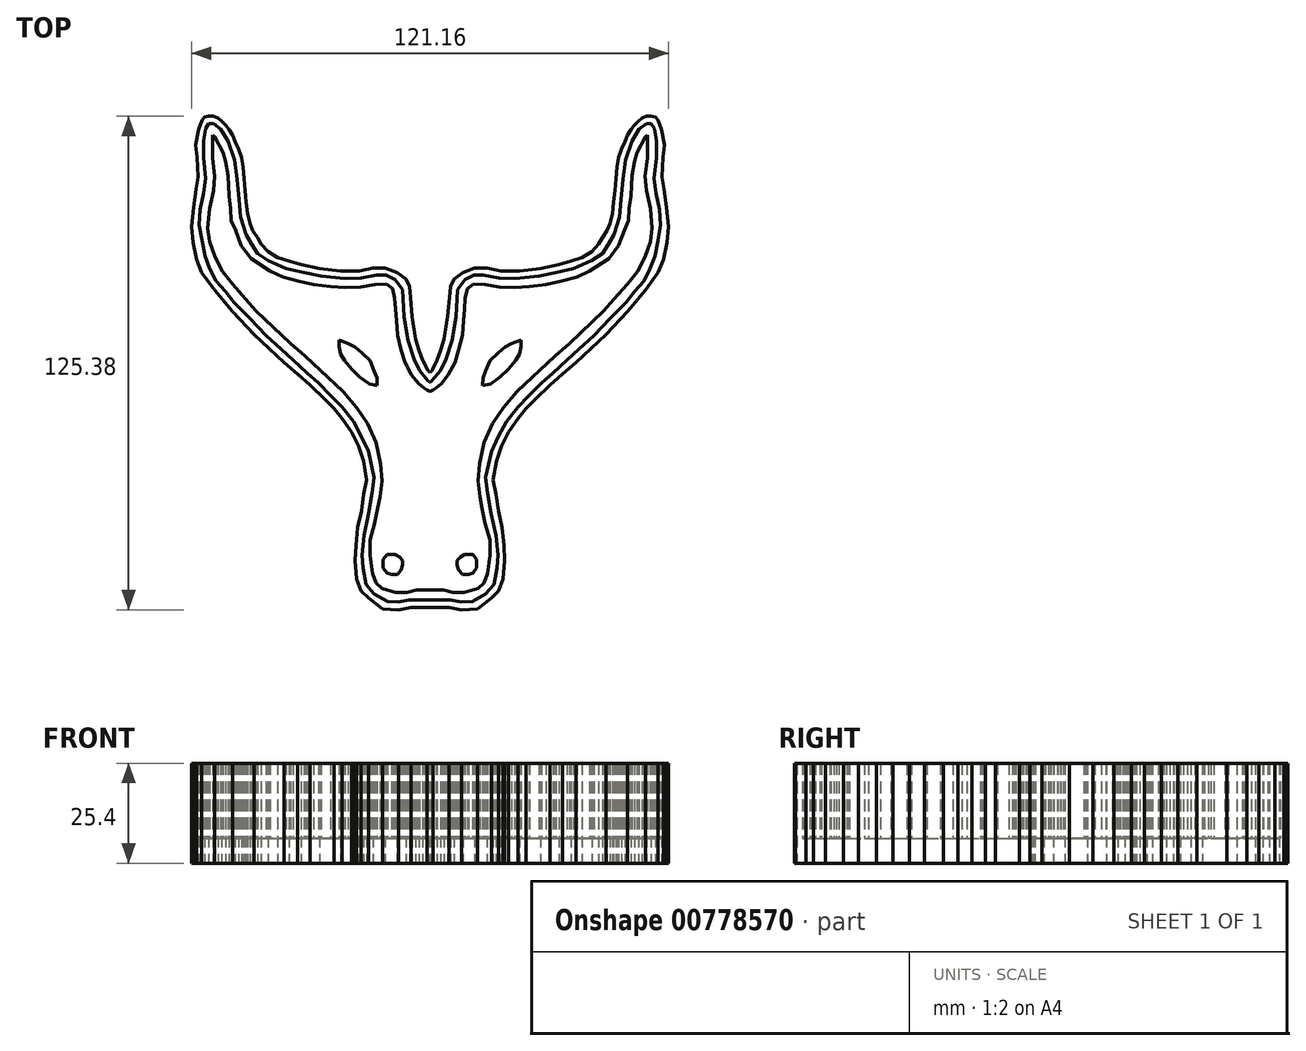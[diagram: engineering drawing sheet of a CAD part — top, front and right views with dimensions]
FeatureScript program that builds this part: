
annotation { "Feature Type Name" : "Feature", "Feature Type Description" : "" }
export const myFeature = defineFeature(function(context is Context, id is Id, definition is map)
    precondition{}
    {
        {
            var Q0;
            Q0=qCreatedBy(makeId("Top.planeOp"),FACE);
            var sketch = newSketch(context, id + "F0", { "sketchPlane" : qUnion([Q0])});
            skLineSegment(sketch, "E0", {"start": v(0, -62.65) * mm, "end": v(0.74, -62.65) * mm});
            skLineSegment(sketch, "E1", {"start": v(0.74, -62.65) * mm, "end": v(4.87, -62.73) * mm});
            skLineSegment(sketch, "E2", {"start": v(4.87, -62.73) * mm, "end": v(7.96, -63.29) * mm});
            skLineSegment(sketch, "E3", {"start": v(7.96, -63.29) * mm, "end": v(12.06, -63.03) * mm});
            skLineSegment(sketch, "E4", {"start": v(12.06, -63.03) * mm, "end": v(15.62, -60.34) * mm});
            skLineSegment(sketch, "E5", {"start": v(15.62, -60.34) * mm, "end": v(17.47, -58.47) * mm});
            skLineSegment(sketch, "E6", {"start": v(17.47, -58.47) * mm, "end": v(18.6, -55.45) * mm});
            skLineSegment(sketch, "E7", {"start": v(18.6, -55.45) * mm, "end": v(19, -50.76) * mm});
            skLineSegment(sketch, "E8", {"start": v(19, -50.76) * mm, "end": v(18.78, -46.99) * mm});
            skLineSegment(sketch, "E9", {"start": v(18.78, -46.99) * mm, "end": v(18.36, -42.4) * mm});
            skLineSegment(sketch, "E10", {"start": v(18.36, -42.4) * mm, "end": v(17.38, -38.24) * mm});
            skLineSegment(sketch, "E11", {"start": v(17.38, -38.24) * mm, "end": v(16.84, -34.03) * mm});
            skLineSegment(sketch, "E12", {"start": v(16.84, -34.03) * mm, "end": v(16.08, -30.27) * mm});
            skLineSegment(sketch, "E13", {"start": v(16.08, -30.27) * mm, "end": v(16.93, -25.47) * mm});
            skLineSegment(sketch, "E14", {"start": v(16.93, -25.47) * mm, "end": v(18.14, -21.7) * mm});
            skLineSegment(sketch, "E15", {"start": v(18.14, -21.7) * mm, "end": v(19.93, -18.19) * mm});
            skLineSegment(sketch, "E16", {"start": v(19.93, -18.19) * mm, "end": v(22.34, -14.72) * mm});
            skLineSegment(sketch, "E17", {"start": v(22.34, -14.72) * mm, "end": v(24.35, -12.2) * mm});
            skLineSegment(sketch, "E18", {"start": v(24.35, -12.2) * mm, "end": v(26.71, -9.89) * mm});
            skLineSegment(sketch, "E19", {"start": v(26.71, -9.89) * mm, "end": v(30.5, -6.18) * mm});
            skLineSegment(sketch, "E20", {"start": v(30.5, -6.18) * mm, "end": v(33.6, -3.4) * mm});
            skLineSegment(sketch, "E21", {"start": v(33.6, -3.4) * mm, "end": v(37.06, -0.45) * mm});
            skLineSegment(sketch, "E22", {"start": v(37.06, -0.45) * mm, "end": v(44.75, 6.6) * mm});
            skLineSegment(sketch, "E23", {"start": v(44.75, 6.6) * mm, "end": v(50.18, 12.54) * mm});
            skLineSegment(sketch, "E24", {"start": v(50.18, 12.54) * mm, "end": v(54.75, 17.93) * mm});
            skLineSegment(sketch, "E25", {"start": v(54.75, 17.93) * mm, "end": v(57.98, 22.34) * mm});
            skLineSegment(sketch, "E26", {"start": v(57.98, 22.34) * mm, "end": v(59.34, 25.63) * mm});
            skLineSegment(sketch, "E27", {"start": v(59.34, 25.63) * mm, "end": v(60.16, 30.02) * mm});
            skLineSegment(sketch, "E28", {"start": v(60.16, 30.02) * mm, "end": v(60.58, 34.11) * mm});
            skLineSegment(sketch, "E29", {"start": v(60.58, 34.11) * mm, "end": v(60.1, 38.93) * mm});
            skLineSegment(sketch, "E30", {"start": v(60.1, 38.93) * mm, "end": v(59.4, 43.55) * mm});
            skLineSegment(sketch, "E31", {"start": v(59.4, 43.55) * mm, "end": v(58.97, 46.63) * mm});
            skLineSegment(sketch, "E32", {"start": v(58.97, 46.63) * mm, "end": v(59.15, 51.67) * mm});
            skLineSegment(sketch, "E33", {"start": v(59.15, 51.67) * mm, "end": v(59.6, 54.77) * mm});
            skLineSegment(sketch, "E34", {"start": v(59.6, 54.77) * mm, "end": v(58.85, 58.77) * mm});
            skLineSegment(sketch, "E35", {"start": v(58.85, 58.77) * mm, "end": v(57.94, 61.11) * mm});
            skLineSegment(sketch, "E36", {"start": v(57.94, 61.11) * mm, "end": v(57.23, 61.84) * mm});
            skLineSegment(sketch, "E37", {"start": v(57.23, 61.84) * mm, "end": v(56.19, 62.09) * mm});
            skLineSegment(sketch, "E38", {"start": v(56.19, 62.09) * mm, "end": v(55.06, 62.09) * mm});
            skLineSegment(sketch, "E39", {"start": v(55.06, 62.09) * mm, "end": v(53.9, 61.63) * mm});
            skLineSegment(sketch, "E40", {"start": v(53.9, 61.63) * mm, "end": v(52.95, 60.92) * mm});
            skLineSegment(sketch, "E41", {"start": v(52.95, 60.92) * mm, "end": v(51.9, 59.9) * mm});
            skLineSegment(sketch, "E42", {"start": v(51.9, 59.9) * mm, "end": v(51.01, 58.77) * mm});
            skLineSegment(sketch, "E43", {"start": v(51.01, 58.77) * mm, "end": v(50.17, 57.35) * mm});
            skLineSegment(sketch, "E44", {"start": v(50.17, 57.35) * mm, "end": v(49.52, 55.7) * mm});
            skLineSegment(sketch, "E45", {"start": v(49.52, 55.7) * mm, "end": v(48.62, 53.78) * mm});
            skLineSegment(sketch, "E46", {"start": v(48.62, 53.78) * mm, "end": v(47.9, 51.57) * mm});
            skLineSegment(sketch, "E47", {"start": v(47.9, 51.57) * mm, "end": v(47.46, 49.14) * mm});
            skLineSegment(sketch, "E48", {"start": v(47.46, 49.14) * mm, "end": v(47.2, 46.3) * mm});
            skLineSegment(sketch, "E49", {"start": v(47.2, 46.3) * mm, "end": v(46.94, 43.22) * mm});
            skLineSegment(sketch, "E50", {"start": v(46.94, 43.22) * mm, "end": v(46.7, 40.3) * mm});
            skLineSegment(sketch, "E51", {"start": v(46.7, 40.3) * mm, "end": v(46.39, 37.4) * mm});
            skLineSegment(sketch, "E52", {"start": v(46.39, 37.4) * mm, "end": v(45.73, 34.8) * mm});
            skLineSegment(sketch, "E53", {"start": v(45.73, 34.8) * mm, "end": v(45.03, 33.04) * mm});
            skLineSegment(sketch, "E54", {"start": v(45.03, 33.04) * mm, "end": v(43.83, 31.24) * mm});
            skLineSegment(sketch, "E55", {"start": v(43.83, 31.24) * mm, "end": v(42.87, 29.66) * mm});
            skLineSegment(sketch, "E56", {"start": v(42.87, 29.66) * mm, "end": v(41.16, 27.69) * mm});
            skLineSegment(sketch, "E57", {"start": v(41.16, 27.69) * mm, "end": v(38.68, 26.24) * mm});
            skLineSegment(sketch, "E58", {"start": v(38.68, 26.24) * mm, "end": v(35.85, 25.34) * mm});
            skLineSegment(sketch, "E59", {"start": v(35.85, 25.34) * mm, "end": v(32.72, 24.46) * mm});
            skLineSegment(sketch, "E60", {"start": v(32.72, 24.46) * mm, "end": v(28.06, 23.4) * mm});
            skLineSegment(sketch, "E61", {"start": v(28.06, 23.4) * mm, "end": v(22.72, 22.8) * mm});
            skLineSegment(sketch, "E62", {"start": v(22.72, 22.8) * mm, "end": v(18.07, 22.8) * mm});
            skLineSegment(sketch, "E63", {"start": v(18.07, 22.8) * mm, "end": v(14.47, 23.58) * mm});
            skLineSegment(sketch, "E64", {"start": v(14.47, 23.58) * mm, "end": v(11.36, 23.58) * mm});
            skLineSegment(sketch, "E65", {"start": v(11.36, 23.58) * mm, "end": v(8.37, 22.4) * mm});
            skLineSegment(sketch, "E66", {"start": v(8.37, 22.4) * mm, "end": v(6.11, 20.67) * mm});
            skLineSegment(sketch, "E67", {"start": v(6.11, 20.67) * mm, "end": v(5.22, 18.85) * mm});
            skLineSegment(sketch, "E68", {"start": v(5.22, 18.85) * mm, "end": v(4.92, 15.98) * mm});
            skLineSegment(sketch, "E69", {"start": v(4.52, 11.15) * mm, "end": v(3.62, 5.47) * mm});
            skLineSegment(sketch, "E70", {"start": v(3.62, 5.47) * mm, "end": v(2.73, 2.52) * mm});
            skLineSegment(sketch, "E71", {"start": v(2.73, 2.52) * mm, "end": v(1.85, 0.16) * mm});
            skLineSegment(sketch, "E72", {"start": v(1.85, 0.16) * mm, "end": v(0.64, -2.23) * mm});
            skLineSegment(sketch, "E73", {"start": v(0.64, -2.23) * mm, "end": v(0.34, -2.71) * mm});
            skLineSegment(sketch, "E74", {"start": v(0.34, -2.71) * mm, "end": v(0, -2.85) * mm});
            skLineSegment(sketch, "E75", {"start": v(4.52, 11.15) * mm, "end": v(4.92, 15.98) * mm});
            skLineSegment(sketch, "E76", {"start": v(13.4, -6.26) * mm, "end": v(15.4, -5.94) * mm});
            skLineSegment(sketch, "E77", {"start": v(15.4, -5.94) * mm, "end": v(17.85, -4.1) * mm});
            skLineSegment(sketch, "E78", {"start": v(17.85, -4.1) * mm, "end": v(19.98, -2.1) * mm});
            skLineSegment(sketch, "E79", {"start": v(19.98, -2.1) * mm, "end": v(21.74, 0) * mm});
            skLineSegment(sketch, "E80", {"start": v(21.74, 0) * mm, "end": v(22.7, 1.68) * mm});
            skLineSegment(sketch, "E81", {"start": v(22.7, 1.68) * mm, "end": v(23.14, 3.64) * mm});
            skLineSegment(sketch, "E82", {"start": v(23.14, 3.64) * mm, "end": v(23.14, 5.28) * mm});
            skLineSegment(sketch, "E83", {"start": v(23.14, 5.28) * mm, "end": v(20.78, 4.36) * mm});
            skLineSegment(sketch, "E84", {"start": v(20.78, 4.36) * mm, "end": v(19.02, 3.52) * mm});
            skLineSegment(sketch, "E85", {"start": v(19.02, 3.52) * mm, "end": v(17.25, 1.92) * mm});
            skLineSegment(sketch, "E86", {"start": v(17.25, 1.92) * mm, "end": v(15.25, 0) * mm});
            skLineSegment(sketch, "E87", {"start": v(15.25, 0) * mm, "end": v(14.17, -2.57) * mm});
            skLineSegment(sketch, "E88", {"start": v(14.17, -2.57) * mm, "end": v(13.48, -4.42) * mm});
            skLineSegment(sketch, "E89", {"start": v(13.48, -4.42) * mm, "end": v(13.4, -6.26) * mm});
            skLineSegment(sketch, "E90", {"start": v(8.83, -49.27) * mm, "end": v(10.95, -49.27) * mm});
            skLineSegment(sketch, "E91", {"start": v(10.95, -49.27) * mm, "end": v(11.86, -50.52) * mm});
            skLineSegment(sketch, "E92", {"start": v(11.86, -50.52) * mm, "end": v(11.86, -52.64) * mm});
            skLineSegment(sketch, "E93", {"start": v(11.86, -52.64) * mm, "end": v(10.95, -54) * mm});
            skLineSegment(sketch, "E94", {"start": v(10.95, -54) * mm, "end": v(9.74, -54.3) * mm});
            skLineSegment(sketch, "E95", {"start": v(9.74, -54.3) * mm, "end": v(8.22, -54.3) * mm});
            skLineSegment(sketch, "E96", {"start": v(8.22, -54.3) * mm, "end": v(7.31, -53.18) * mm});
            skLineSegment(sketch, "E97", {"start": v(7.31, -53.18) * mm, "end": v(6.9, -51.93) * mm});
            skLineSegment(sketch, "E98", {"start": v(6.9, -51.93) * mm, "end": v(6.9, -50.72) * mm});
            skLineSegment(sketch, "E99", {"start": v(6.9, -50.72) * mm, "end": v(7.75, -49.88) * mm});
            skLineSegment(sketch, "E100", {"start": v(7.75, -49.88) * mm, "end": v(8.83, -49.27) * mm});
            skLineSegment(sketch, "E101", {"start": v(0, -58.26) * mm, "end": v(3.39, -58.26) * mm});
            skLineSegment(sketch, "E102", {"start": v(3.39, -58.26) * mm, "end": v(5.83, -58.91) * mm});
            skLineSegment(sketch, "E103", {"start": v(5.83, -58.91) * mm, "end": v(8.72, -58.91) * mm});
            skLineSegment(sketch, "E104", {"start": v(8.72, -58.91) * mm, "end": v(12.18, -57.92) * mm});
            skLineSegment(sketch, "E105", {"start": v(12.18, -57.92) * mm, "end": v(13.68, -56.45) * mm});
            skLineSegment(sketch, "E106", {"start": v(13.68, -56.45) * mm, "end": v(14.61, -54.04) * mm});
            skLineSegment(sketch, "E107", {"start": v(14.61, -54.04) * mm, "end": v(15.24, -49.5) * mm});
            skLineSegment(sketch, "E108", {"start": v(15.24, -49.5) * mm, "end": v(15.24, -45.5) * mm});
            skLineSegment(sketch, "E109", {"start": v(15.24, -45.5) * mm, "end": v(14.06, -41.39) * mm});
            skLineSegment(sketch, "E110", {"start": v(14.06, -41.39) * mm, "end": v(13.28, -37.6) * mm});
            skLineSegment(sketch, "E111", {"start": v(13.28, -37.6) * mm, "end": v(12.71, -34.68) * mm});
            skLineSegment(sketch, "E112", {"start": v(12.71, -34.68) * mm, "end": v(12.18, -30.57) * mm});
            skLineSegment(sketch, "E113", {"start": v(12.18, -30.57) * mm, "end": v(12.57, -26.2) * mm});
            skLineSegment(sketch, "E114", {"start": v(12.57, -26.2) * mm, "end": v(13.68, -20.73) * mm});
            skLineSegment(sketch, "E115", {"start": v(13.68, -20.73) * mm, "end": v(15.92, -16) * mm});
            skLineSegment(sketch, "E116", {"start": v(15.92, -16) * mm, "end": v(18.67, -11.86) * mm});
            skLineSegment(sketch, "E117", {"start": v(18.67, -11.86) * mm, "end": v(22.07, -7.86) * mm});
            skLineSegment(sketch, "E118", {"start": v(22.07, -7.86) * mm, "end": v(25.8, -4.35) * mm});
            skLineSegment(sketch, "E119", {"start": v(25.8, -4.35) * mm, "end": v(28.59, -1.74) * mm});
            skLineSegment(sketch, "E120", {"start": v(28.59, -1.74) * mm, "end": v(31.74, 1.23) * mm});
            skLineSegment(sketch, "E121", {"start": v(31.74, 1.23) * mm, "end": v(35.39, 4.35) * mm});
            skLineSegment(sketch, "E122", {"start": v(35.39, 4.35) * mm, "end": v(39.8, 8.5) * mm});
            skLineSegment(sketch, "E123", {"start": v(39.8, 8.5) * mm, "end": v(44.15, 12.58) * mm});
            skLineSegment(sketch, "E124", {"start": v(44.15, 12.58) * mm, "end": v(46.78, 15.6) * mm});
            skLineSegment(sketch, "E125", {"start": v(46.78, 15.6) * mm, "end": v(50.13, 19.4) * mm});
            skLineSegment(sketch, "E126", {"start": v(50.13, 19.4) * mm, "end": v(52.7, 22.66) * mm});
            skLineSegment(sketch, "E127", {"start": v(52.7, 22.66) * mm, "end": v(54.6, 26.35) * mm});
            skLineSegment(sketch, "E128", {"start": v(54.6, 26.35) * mm, "end": v(56.02, 30.32) * mm});
            skLineSegment(sketch, "E129", {"start": v(56.02, 30.32) * mm, "end": v(56.45, 33.75) * mm});
            skLineSegment(sketch, "E130", {"start": v(56.45, 33.75) * mm, "end": v(56.02, 38.6) * mm});
            skLineSegment(sketch, "E131", {"start": v(56.02, 38.6) * mm, "end": v(55, 43.24) * mm});
            skLineSegment(sketch, "E132", {"start": v(55, 43.24) * mm, "end": v(54.69, 46.85) * mm});
            skLineSegment(sketch, "E133", {"start": v(54.69, 46.85) * mm, "end": v(55.29, 51.46) * mm});
            skLineSegment(sketch, "E134", {"start": v(55.29, 51.46) * mm, "end": v(55.29, 54.8) * mm});
            skLineSegment(sketch, "E135", {"start": v(55.29, 54.8) * mm, "end": v(55.29, 57.3) * mm});
            skLineSegment(sketch, "E136", {"start": v(55.29, 57.3) * mm, "end": v(54.78, 56.96) * mm});
            skLineSegment(sketch, "E137", {"start": v(54.78, 56.96) * mm, "end": v(53.87, 55.29) * mm});
            skLineSegment(sketch, "E138", {"start": v(53.87, 55.29) * mm, "end": v(52.55, 52.86) * mm});
            skLineSegment(sketch, "E139", {"start": v(52.55, 52.86) * mm, "end": v(51.97, 50.53) * mm});
            skLineSegment(sketch, "E140", {"start": v(51.97, 50.53) * mm, "end": v(51.3, 46.98) * mm});
            skLineSegment(sketch, "E141", {"start": v(51.3, 46.98) * mm, "end": v(51.02, 41.84) * mm});
            skLineSegment(sketch, "E142", {"start": v(51.02, 41.84) * mm, "end": v(50.62, 38.65) * mm});
            skLineSegment(sketch, "E143", {"start": v(50.62, 38.65) * mm, "end": v(50.46, 35.6) * mm});
            skLineSegment(sketch, "E144", {"start": v(50.46, 35.6) * mm, "end": v(49.38, 33.15) * mm});
            skLineSegment(sketch, "E145", {"start": v(49.38, 33.15) * mm, "end": v(47.94, 29.21) * mm});
            skLineSegment(sketch, "E146", {"start": v(47.94, 29.21) * mm, "end": v(45.51, 25.93) * mm});
            skLineSegment(sketch, "E147", {"start": v(45.51, 25.93) * mm, "end": v(40.56, 22.72) * mm});
            skLineSegment(sketch, "E148", {"start": v(40.56, 22.72) * mm, "end": v(37.33, 21.28) * mm});
            skLineSegment(sketch, "E149", {"start": v(37.33, 21.28) * mm, "end": v(33.44, 20.23) * mm});
            skLineSegment(sketch, "E150", {"start": v(33.44, 20.23) * mm, "end": v(29.54, 19.3) * mm});
            skLineSegment(sketch, "E151", {"start": v(29.54, 19.3) * mm, "end": v(25.31, 18.86) * mm});
            skLineSegment(sketch, "E152", {"start": v(25.31, 18.86) * mm, "end": v(21.54, 18.56) * mm});
            skLineSegment(sketch, "E153", {"start": v(21.54, 18.56) * mm, "end": v(17.66, 18.76) * mm});
            skLineSegment(sketch, "E154", {"start": v(17.66, 18.76) * mm, "end": v(13.99, 19.32) * mm});
            skLineSegment(sketch, "E155", {"start": v(13.99, 19.32) * mm, "end": v(11.07, 19.47) * mm});
            skLineSegment(sketch, "E156", {"start": v(11.07, 19.47) * mm, "end": v(9.48, 18.3) * mm});
            skLineSegment(sketch, "E157", {"start": v(9.48, 18.3) * mm, "end": v(8.94, 15.89) * mm});
            skLineSegment(sketch, "E158", {"start": v(8.94, 15.89) * mm, "end": v(8.8, 13.1) * mm});
            skLineSegment(sketch, "E159", {"start": v(8.8, 13.1) * mm, "end": v(8.48, 10.24) * mm});
            skLineSegment(sketch, "E160", {"start": v(8.48, 10.24) * mm, "end": v(8.28, 6.5) * mm});
            skLineSegment(sketch, "E161", {"start": v(8.28, 6.5) * mm, "end": v(7.31, 2.66) * mm});
            skLineSegment(sketch, "E162", {"start": v(7.31, 2.66) * mm, "end": v(6.37, -0.49) * mm});
            skLineSegment(sketch, "E163", {"start": v(6.37, -0.49) * mm, "end": v(4.65, -3.6) * mm});
            skLineSegment(sketch, "E164", {"start": v(4.65, -3.6) * mm, "end": v(2.89, -5.84) * mm});
            skLineSegment(sketch, "E165", {"start": v(2.89, -5.84) * mm, "end": v(1.52, -6.98) * mm});
            skLineSegment(sketch, "E166", {"start": v(1.52, -6.98) * mm, "end": v(0.76, -7.52) * mm});
            skLineSegment(sketch, "E167", {"start": v(0.76, -7.52) * mm, "end": v(0, -7.9) * mm});
            skLineSegment(sketch, "E168", {"start": v(0, 69.58) * mm, "end": v(0, -68.29) * mm, "construction": true});
            skLineSegment(sketch, "E169.MirrorCS", {"start": v(-0.64, -2.23) * mm, "end": v(-0.34, -2.71) * mm});
            skLineSegment(sketch, "E170.MirrorCS", {"start": v(-0.34, -2.71) * mm, "end": v(0, -2.85) * mm});
            skLineSegment(sketch, "E171.MirrorCS", {"start": v(-1.85, 0.16) * mm, "end": v(-0.64, -2.23) * mm});
            skLineSegment(sketch, "E172.MirrorCS", {"start": v(-55.29, 57.3) * mm, "end": v(-54.78, 56.96) * mm});
            skLineSegment(sketch, "E173.MirrorCS", {"start": v(-9.48, 18.3) * mm, "end": v(-8.94, 15.89) * mm});
            skLineSegment(sketch, "E174.MirrorCS", {"start": v(-56.19, 62.09) * mm, "end": v(-55.06, 62.09) * mm});
            skLineSegment(sketch, "E175.MirrorCS", {"start": v(-52.95, 60.92) * mm, "end": v(-51.9, 59.9) * mm});
            skLineSegment(sketch, "E176.MirrorCS", {"start": v(-55.06, 62.09) * mm, "end": v(-53.9, 61.63) * mm});
            skLineSegment(sketch, "E177.MirrorCS", {"start": v(-53.9, 61.63) * mm, "end": v(-52.95, 60.92) * mm});
            skLineSegment(sketch, "E178.MirrorCS", {"start": v(-51.9, 59.9) * mm, "end": v(-51.01, 58.77) * mm});
            skLineSegment(sketch, "E179.MirrorCS", {"start": v(-57.98, 22.34) * mm, "end": v(-59.34, 25.63) * mm});
            skLineSegment(sketch, "E180.MirrorCS", {"start": v(-8.83, -49.27) * mm, "end": v(-10.95, -49.27) * mm});
            skLineSegment(sketch, "E181.MirrorCS", {"start": v(-51.01, 58.77) * mm, "end": v(-50.17, 57.35) * mm});
            skLineSegment(sketch, "E182.MirrorCS", {"start": v(-10.95, -49.27) * mm, "end": v(-11.86, -50.52) * mm});
            skLineSegment(sketch, "E183.MirrorCS", {"start": v(-12.06, -63.03) * mm, "end": v(-15.62, -60.34) * mm});
            skLineSegment(sketch, "E184.MirrorCS", {"start": v(-15.62, -60.34) * mm, "end": v(-17.47, -58.47) * mm});
            skLineSegment(sketch, "E185.MirrorCS", {"start": v(-11.86, -50.52) * mm, "end": v(-11.86, -52.64) * mm});
            skLineSegment(sketch, "E186.MirrorCS", {"start": v(-17.47, -58.47) * mm, "end": v(-18.6, -55.45) * mm});
            skLineSegment(sketch, "E187.MirrorCS", {"start": v(-18.6, -55.45) * mm, "end": v(-19, -50.76) * mm});
            skLineSegment(sketch, "E188.MirrorCS", {"start": v(-50.17, 57.35) * mm, "end": v(-49.52, 55.7) * mm});
            skLineSegment(sketch, "E189.MirrorCS", {"start": v(-2.89, -5.84) * mm, "end": v(-1.52, -6.98) * mm});
            skLineSegment(sketch, "E190.MirrorCS", {"start": v(-16.08, -30.27) * mm, "end": v(-16.93, -25.47) * mm});
            skLineSegment(sketch, "E191.MirrorCS", {"start": v(-49.52, 55.7) * mm, "end": v(-48.62, 53.78) * mm});
            skLineSegment(sketch, "E192.MirrorCS", {"start": v(-1.52, -6.98) * mm, "end": v(-0.76, -7.52) * mm});
            skLineSegment(sketch, "E193.MirrorCS", {"start": v(-47.46, 49.14) * mm, "end": v(-47.2, 46.3) * mm});
            skLineSegment(sketch, "E194.MirrorCS", {"start": v(-11.36, 23.58) * mm, "end": v(-8.37, 22.4) * mm});
            skLineSegment(sketch, "E195.MirrorCS", {"start": v(-47.2, 46.3) * mm, "end": v(-46.94, 43.22) * mm});
            skLineSegment(sketch, "E196.MirrorCS", {"start": v(-0.76, -7.52) * mm, "end": v(0, -7.9) * mm});
            skLineSegment(sketch, "E197.MirrorCS", {"start": v(-54.78, 56.96) * mm, "end": v(-53.87, 55.29) * mm});
            skLineSegment(sketch, "E198.MirrorCS", {"start": v(-12.18, -57.92) * mm, "end": v(-13.68, -56.45) * mm});
            skLineSegment(sketch, "E199.MirrorCS", {"start": v(-48.62, 53.78) * mm, "end": v(-47.9, 51.57) * mm});
            skLineSegment(sketch, "E200.MirrorCS", {"start": v(-11.07, 19.47) * mm, "end": v(-9.48, 18.3) * mm});
            skLineSegment(sketch, "E201.MirrorCS", {"start": v(-51.97, 50.53) * mm, "end": v(-51.3, 46.98) * mm});
            skLineSegment(sketch, "E202.MirrorCS", {"start": v(-47.9, 51.57) * mm, "end": v(-47.46, 49.14) * mm});
            skLineSegment(sketch, "E203.MirrorCS", {"start": v(-8.37, 22.4) * mm, "end": v(-6.11, 20.67) * mm});
            skLineSegment(sketch, "E204.MirrorCS", {"start": v(-46.94, 43.22) * mm, "end": v(-46.7, 40.3) * mm});
            skLineSegment(sketch, "E205.MirrorCS", {"start": v(-30.5, -6.18) * mm, "end": v(-33.6, -3.4) * mm});
            skLineSegment(sketch, "E206.MirrorCS", {"start": v(-57.94, 61.11) * mm, "end": v(-57.23, 61.84) * mm});
            skLineSegment(sketch, "E207.MirrorCS", {"start": v(-57.23, 61.84) * mm, "end": v(-56.19, 62.09) * mm});
            skLineSegment(sketch, "E208.MirrorCS", {"start": v(-46.7, 40.3) * mm, "end": v(-46.39, 37.4) * mm});
            skLineSegment(sketch, "E209.MirrorCS", {"start": v(-52.55, 52.86) * mm, "end": v(-51.97, 50.53) * mm});
            skLineSegment(sketch, "E210.MirrorCS", {"start": v(-14.61, -54.04) * mm, "end": v(-15.24, -49.5) * mm});
            skLineSegment(sketch, "E211.MirrorCS", {"start": v(-13.68, -56.45) * mm, "end": v(-14.61, -54.04) * mm});
            skLineSegment(sketch, "E212.MirrorCS", {"start": v(-53.87, 55.29) * mm, "end": v(-52.55, 52.86) * mm});
            skLineSegment(sketch, "E213.MirrorCS", {"start": v(-41.16, 27.69) * mm, "end": v(-38.68, 26.24) * mm});
            skLineSegment(sketch, "E214.MirrorCS", {"start": v(-42.87, 29.66) * mm, "end": v(-41.16, 27.69) * mm});
            skLineSegment(sketch, "E215.MirrorCS", {"start": v(-38.68, 26.24) * mm, "end": v(-35.85, 25.34) * mm});
            skLineSegment(sketch, "E216.MirrorCS", {"start": v(0, -62.65) * mm, "end": v(-0.74, -62.65) * mm});
            skLineSegment(sketch, "E217.MirrorCS", {"start": v(-19, -50.76) * mm, "end": v(-18.78, -46.99) * mm});
            skLineSegment(sketch, "E218.MirrorCS", {"start": v(-11.86, -52.64) * mm, "end": v(-10.95, -54) * mm});
            skLineSegment(sketch, "E219.MirrorCS", {"start": v(-15.24, -49.5) * mm, "end": v(-15.24, -45.5) * mm});
            skLineSegment(sketch, "E220.MirrorCS", {"start": v(-58.85, 58.77) * mm, "end": v(-57.94, 61.11) * mm});
            skLineSegment(sketch, "E221.MirrorCS", {"start": v(-4.52, 11.15) * mm, "end": v(-3.62, 5.47) * mm});
            skLineSegment(sketch, "E222.MirrorCS", {"start": v(-15.24, -45.5) * mm, "end": v(-14.06, -41.39) * mm});
            skLineSegment(sketch, "E223.MirrorCS", {"start": v(-51.3, 46.98) * mm, "end": v(-51.02, 41.84) * mm});
            skLineSegment(sketch, "E224.MirrorCS", {"start": v(-46.78, 15.6) * mm, "end": v(-50.13, 19.4) * mm});
            skLineSegment(sketch, "E225.MirrorCS", {"start": v(-45.03, 33.04) * mm, "end": v(-43.83, 31.24) * mm});
            skLineSegment(sketch, "E226.MirrorCS", {"start": v(-37.06, -0.45) * mm, "end": v(-44.75, 6.6) * mm});
            skLineSegment(sketch, "E227.MirrorCS", {"start": v(-17.25, 1.92) * mm, "end": v(-15.25, 0) * mm});
            skLineSegment(sketch, "E228.MirrorCS", {"start": v(-3.62, 5.47) * mm, "end": v(-2.73, 2.52) * mm});
            skLineSegment(sketch, "E229.MirrorCS", {"start": v(-14.06, -41.39) * mm, "end": v(-13.28, -37.6) * mm});
            skLineSegment(sketch, "E230.MirrorCS", {"start": v(-8.94, 15.89) * mm, "end": v(-8.8, 13.1) * mm});
            skLineSegment(sketch, "E231.MirrorCS", {"start": v(-51.02, 41.84) * mm, "end": v(-50.62, 38.65) * mm});
            skLineSegment(sketch, "E232.MirrorCS", {"start": v(-50.13, 19.4) * mm, "end": v(-52.7, 22.66) * mm});
            skLineSegment(sketch, "E233.MirrorCS", {"start": v(-54.75, 17.93) * mm, "end": v(-57.98, 22.34) * mm});
            skLineSegment(sketch, "E234.MirrorCS", {"start": v(-43.83, 31.24) * mm, "end": v(-42.87, 29.66) * mm});
            skLineSegment(sketch, "E235.MirrorCS", {"start": v(-44.75, 6.6) * mm, "end": v(-50.18, 12.54) * mm});
            skLineSegment(sketch, "E236.MirrorCS", {"start": v(-13.48, -4.42) * mm, "end": v(-13.4, -6.26) * mm});
            skLineSegment(sketch, "E237.MirrorCS", {"start": v(-56.02, 30.32) * mm, "end": v(-56.45, 33.75) * mm});
            skLineSegment(sketch, "E238.MirrorCS", {"start": v(-12.18, -30.57) * mm, "end": v(-12.57, -26.2) * mm});
            skLineSegment(sketch, "E239.MirrorCS", {"start": v(-8.28, 6.5) * mm, "end": v(-7.31, 2.66) * mm});
            skLineSegment(sketch, "E240.MirrorCS", {"start": v(-15.25, 0) * mm, "end": v(-14.17, -2.57) * mm});
            skLineSegment(sketch, "E241.MirrorCS", {"start": v(-2.73, 2.52) * mm, "end": v(-1.85, 0.16) * mm});
            skLineSegment(sketch, "E242.MirrorCS", {"start": v(-13.28, -37.6) * mm, "end": v(-12.71, -34.68) * mm});
            skLineSegment(sketch, "E243.MirrorCS", {"start": v(-8.8, 13.1) * mm, "end": v(-8.48, 10.24) * mm});
            skLineSegment(sketch, "E244.MirrorCS", {"start": v(-50.62, 38.65) * mm, "end": v(-50.46, 35.6) * mm});
            skLineSegment(sketch, "E245.MirrorCS", {"start": v(-52.7, 22.66) * mm, "end": v(-54.6, 26.35) * mm});
            skLineSegment(sketch, "E246.MirrorCS", {"start": v(-49.38, 33.15) * mm, "end": v(-47.94, 29.21) * mm});
            skLineSegment(sketch, "E247.MirrorCS", {"start": v(-50.18, 12.54) * mm, "end": v(-54.75, 17.93) * mm});
            skLineSegment(sketch, "E248.MirrorCS", {"start": v(-14.17, -2.57) * mm, "end": v(-13.48, -4.42) * mm});
            skLineSegment(sketch, "E249.MirrorCS", {"start": v(-56.45, 33.75) * mm, "end": v(-56.02, 38.6) * mm});
            skLineSegment(sketch, "E250.MirrorCS", {"start": v(-12.57, -26.2) * mm, "end": v(-13.68, -20.73) * mm});
            skLineSegment(sketch, "E251.MirrorCS", {"start": v(-7.31, 2.66) * mm, "end": v(-6.37, -0.49) * mm});
            skLineSegment(sketch, "E252.MirrorCS", {"start": v(-12.71, -34.68) * mm, "end": v(-12.18, -30.57) * mm});
            skLineSegment(sketch, "E253.MirrorCS", {"start": v(-8.48, 10.24) * mm, "end": v(-8.28, 6.5) * mm});
            skLineSegment(sketch, "E254.MirrorCS", {"start": v(-50.46, 35.6) * mm, "end": v(-49.38, 33.15) * mm});
            skLineSegment(sketch, "E255.MirrorCS", {"start": v(-54.6, 26.35) * mm, "end": v(-56.02, 30.32) * mm});
            skLineSegment(sketch, "E256.MirrorCS", {"start": v(-47.94, 29.21) * mm, "end": v(-45.51, 25.93) * mm});
            skLineSegment(sketch, "E257.MirrorCS", {"start": v(-18.78, -46.99) * mm, "end": v(-18.36, -42.4) * mm});
            skLineSegment(sketch, "E258.MirrorCS", {"start": v(-18.36, -42.4) * mm, "end": v(-17.38, -38.24) * mm});
            skLineSegment(sketch, "E259.MirrorCS", {"start": v(-17.38, -38.24) * mm, "end": v(-16.84, -34.03) * mm});
            skLineSegment(sketch, "E260.MirrorCS", {"start": v(-4.52, 11.15) * mm, "end": v(-4.92, 15.98) * mm});
            skLineSegment(sketch, "E261.MirrorCS", {"start": v(-35.85, 25.34) * mm, "end": v(-32.72, 24.46) * mm});
            skLineSegment(sketch, "E262.MirrorCS", {"start": v(-59.34, 25.63) * mm, "end": v(-60.16, 30.02) * mm});
            skLineSegment(sketch, "E263.MirrorCS", {"start": v(-56.02, 38.6) * mm, "end": v(-55, 43.24) * mm});
            skLineSegment(sketch, "E264.MirrorCS", {"start": v(-13.68, -20.73) * mm, "end": v(-15.92, -16) * mm});
            skLineSegment(sketch, "E265.MirrorCS", {"start": v(-6.37, -0.49) * mm, "end": v(-4.65, -3.6) * mm});
            skLineSegment(sketch, "E266.MirrorCS", {"start": v(-0.74, -62.65) * mm, "end": v(-4.87, -62.73) * mm});
            skLineSegment(sketch, "E267.MirrorCS", {"start": v(-4.87, -62.73) * mm, "end": v(-7.96, -63.29) * mm});
            skLineSegment(sketch, "E268.MirrorCS", {"start": v(-7.96, -63.29) * mm, "end": v(-12.06, -63.03) * mm});
            skLineSegment(sketch, "E269.MirrorCS", {"start": v(-45.51, 25.93) * mm, "end": v(-40.56, 22.72) * mm});
            skLineSegment(sketch, "E270.MirrorCS", {"start": v(-55, 43.24) * mm, "end": v(-54.69, 46.85) * mm});
            skLineSegment(sketch, "E271.MirrorCS", {"start": v(-15.92, -16) * mm, "end": v(-18.67, -11.86) * mm});
            skLineSegment(sketch, "E272.MirrorCS", {"start": v(-4.65, -3.6) * mm, "end": v(-2.89, -5.84) * mm});
            skLineSegment(sketch, "E273.MirrorCS", {"start": v(-40.56, 22.72) * mm, "end": v(-37.33, 21.28) * mm});
            skLineSegment(sketch, "E274.MirrorCS", {"start": v(-16.84, -34.03) * mm, "end": v(-16.08, -30.27) * mm});
            skLineSegment(sketch, "E275.MirrorCS", {"start": v(-13.4, -6.26) * mm, "end": v(-15.4, -5.94) * mm});
            skLineSegment(sketch, "E276.MirrorCS", {"start": v(-32.72, 24.46) * mm, "end": v(-28.06, 23.4) * mm});
            skLineSegment(sketch, "E277.MirrorCS", {"start": v(-60.16, 30.02) * mm, "end": v(-60.58, 34.11) * mm});
            skLineSegment(sketch, "E278.MirrorCS", {"start": v(-54.69, 46.85) * mm, "end": v(-55.29, 51.46) * mm});
            skLineSegment(sketch, "E279.MirrorCS", {"start": v(-18.67, -11.86) * mm, "end": v(-22.07, -7.86) * mm});
            skLineSegment(sketch, "E280.MirrorCS", {"start": v(0, -58.26) * mm, "end": v(-3.39, -58.26) * mm});
            skLineSegment(sketch, "E281.MirrorCS", {"start": v(-37.33, 21.28) * mm, "end": v(-33.44, 20.23) * mm});
            skLineSegment(sketch, "E282.MirrorCS", {"start": v(-15.4, -5.94) * mm, "end": v(-17.85, -4.1) * mm});
            skLineSegment(sketch, "E283.MirrorCS", {"start": v(-28.06, 23.4) * mm, "end": v(-22.72, 22.8) * mm});
            skLineSegment(sketch, "E284.MirrorCS", {"start": v(-60.58, 34.11) * mm, "end": v(-60.1, 38.93) * mm});
            skLineSegment(sketch, "E285.MirrorCS", {"start": v(-33.44, 20.23) * mm, "end": v(-29.54, 19.3) * mm});
            skLineSegment(sketch, "E286.MirrorCS", {"start": v(-8.22, -54.3) * mm, "end": v(-7.31, -53.18) * mm});
            skLineSegment(sketch, "E287.MirrorCS", {"start": v(-28.59, -1.74) * mm, "end": v(-31.74, 1.23) * mm});
            skLineSegment(sketch, "E288.MirrorCS", {"start": v(-8.72, -58.91) * mm, "end": v(-12.18, -57.92) * mm});
            skLineSegment(sketch, "E289.MirrorCS", {"start": v(-58.97, 46.63) * mm, "end": v(-59.15, 51.67) * mm});
            skLineSegment(sketch, "E290.MirrorCS", {"start": v(-25.31, 18.86) * mm, "end": v(-21.54, 18.56) * mm});
            skLineSegment(sketch, "E291.MirrorCS", {"start": v(-14.47, 23.58) * mm, "end": v(-11.36, 23.58) * mm});
            skLineSegment(sketch, "E292.MirrorCS", {"start": v(-21.74, 0) * mm, "end": v(-22.7, 1.68) * mm});
            skLineSegment(sketch, "E293.MirrorCS", {"start": v(-19.93, -18.19) * mm, "end": v(-22.34, -14.72) * mm});
            skLineSegment(sketch, "E294.MirrorCS", {"start": v(-22.34, -14.72) * mm, "end": v(-24.35, -12.2) * mm});
            skLineSegment(sketch, "E295.MirrorCS", {"start": v(-22.7, 1.68) * mm, "end": v(-23.14, 3.64) * mm});
            skLineSegment(sketch, "E296.MirrorCS", {"start": v(-59.15, 51.67) * mm, "end": v(-59.6, 54.77) * mm});
            skLineSegment(sketch, "E297.MirrorCS", {"start": v(-60.1, 38.93) * mm, "end": v(-59.4, 43.55) * mm});
            skLineSegment(sketch, "E298.MirrorCS", {"start": v(-7.31, -53.18) * mm, "end": v(-6.9, -51.93) * mm});
            skLineSegment(sketch, "E299.MirrorCS", {"start": v(-31.74, 1.23) * mm, "end": v(-35.39, 4.35) * mm});
            skLineSegment(sketch, "E300.MirrorCS", {"start": v(-29.54, 19.3) * mm, "end": v(-25.31, 18.86) * mm});
            skLineSegment(sketch, "E301.MirrorCS", {"start": v(-5.83, -58.91) * mm, "end": v(-8.72, -58.91) * mm});
            skLineSegment(sketch, "E302.MirrorCS", {"start": v(-55.29, 54.8) * mm, "end": v(-55.29, 57.3) * mm});
            skLineSegment(sketch, "E303.MirrorCS", {"start": v(-21.54, 18.56) * mm, "end": v(-17.66, 18.76) * mm});
            skLineSegment(sketch, "E304.MirrorCS", {"start": v(-25.8, -4.35) * mm, "end": v(-28.59, -1.74) * mm});
            skLineSegment(sketch, "E305.MirrorCS", {"start": v(-9.74, -54.3) * mm, "end": v(-8.22, -54.3) * mm});
            skLineSegment(sketch, "E306.MirrorCS", {"start": v(-10.95, -54) * mm, "end": v(-9.74, -54.3) * mm});
            skLineSegment(sketch, "E307.MirrorCS", {"start": v(-55.29, 51.46) * mm, "end": v(-55.29, 54.8) * mm});
            skLineSegment(sketch, "E308.MirrorCS", {"start": v(-22.07, -7.86) * mm, "end": v(-25.8, -4.35) * mm});
            skLineSegment(sketch, "E309.MirrorCS", {"start": v(-22.72, 22.8) * mm, "end": v(-18.07, 22.8) * mm});
            skLineSegment(sketch, "E310.MirrorCS", {"start": v(-3.39, -58.26) * mm, "end": v(-5.83, -58.91) * mm});
            skLineSegment(sketch, "E311.MirrorCS", {"start": v(-16.93, -25.47) * mm, "end": v(-18.14, -21.7) * mm});
            skLineSegment(sketch, "E312.MirrorCS", {"start": v(-59.4, 43.55) * mm, "end": v(-58.97, 46.63) * mm});
            skLineSegment(sketch, "E313.MirrorCS", {"start": v(-44.15, 12.58) * mm, "end": v(-46.78, 15.6) * mm});
            skLineSegment(sketch, "E314.MirrorCS", {"start": v(-5.22, 18.85) * mm, "end": v(-4.92, 15.98) * mm});
            skLineSegment(sketch, "E315.MirrorCS", {"start": v(-20.78, 4.36) * mm, "end": v(-19.02, 3.52) * mm});
            skLineSegment(sketch, "E316.MirrorCS", {"start": v(-17.85, -4.1) * mm, "end": v(-19.98, -2.1) * mm});
            skLineSegment(sketch, "E317.MirrorCS", {"start": v(-7.75, -49.88) * mm, "end": v(-8.83, -49.27) * mm});
            skLineSegment(sketch, "E318.MirrorCS", {"start": v(-24.35, -12.2) * mm, "end": v(-26.71, -9.89) * mm});
            skLineSegment(sketch, "E319.MirrorCS", {"start": v(-23.14, 3.64) * mm, "end": v(-23.14, 5.28) * mm});
            skLineSegment(sketch, "E320.MirrorCS", {"start": v(-59.6, 54.77) * mm, "end": v(-58.85, 58.77) * mm});
            skLineSegment(sketch, "E321.MirrorCS", {"start": v(-19.02, 3.52) * mm, "end": v(-17.25, 1.92) * mm});
            skLineSegment(sketch, "E322.MirrorCS", {"start": v(-46.39, 37.4) * mm, "end": v(-45.73, 34.8) * mm});
            skLineSegment(sketch, "E323.MirrorCS", {"start": v(-33.6, -3.4) * mm, "end": v(-37.06, -0.45) * mm});
            skLineSegment(sketch, "E324.MirrorCS", {"start": v(-45.73, 34.8) * mm, "end": v(-45.03, 33.04) * mm});
            skLineSegment(sketch, "E325.MirrorCS", {"start": v(-18.14, -21.7) * mm, "end": v(-19.93, -18.19) * mm});
            skLineSegment(sketch, "E326.MirrorCS", {"start": v(-19.98, -2.1) * mm, "end": v(-21.74, 0) * mm});
            skLineSegment(sketch, "E327.MirrorCS", {"start": v(-6.11, 20.67) * mm, "end": v(-5.22, 18.85) * mm});
            skLineSegment(sketch, "E328.MirrorCS", {"start": v(-39.8, 8.5) * mm, "end": v(-44.15, 12.58) * mm});
            skLineSegment(sketch, "E329.MirrorCS", {"start": v(-18.07, 22.8) * mm, "end": v(-14.47, 23.58) * mm});
            skLineSegment(sketch, "E330.MirrorCS", {"start": v(-26.71, -9.89) * mm, "end": v(-30.5, -6.18) * mm});
            skLineSegment(sketch, "E331.MirrorCS", {"start": v(-35.39, 4.35) * mm, "end": v(-39.8, 8.5) * mm});
            skLineSegment(sketch, "E332.MirrorCS", {"start": v(-6.9, -51.93) * mm, "end": v(-6.9, -50.72) * mm});
            skLineSegment(sketch, "E333.MirrorCS", {"start": v(-17.66, 18.76) * mm, "end": v(-13.99, 19.32) * mm});
            skLineSegment(sketch, "E334.MirrorCS", {"start": v(-23.14, 5.28) * mm, "end": v(-20.78, 4.36) * mm});
            skLineSegment(sketch, "E335.MirrorCS", {"start": v(-13.99, 19.32) * mm, "end": v(-11.07, 19.47) * mm});
            skLineSegment(sketch, "E336.MirrorCS", {"start": v(-6.9, -50.72) * mm, "end": v(-7.75, -49.88) * mm});
            skLineSegment(sketch, "E337", {"start": v(0, -60.82) * mm, "end": v(2.56, -60.82) * mm});
            skLineSegment(sketch, "E338", {"start": v(2.56, -60.82) * mm, "end": v(5.28, -60.82) * mm});
            skLineSegment(sketch, "E339", {"start": v(5.28, -60.82) * mm, "end": v(7.95, -61.3) * mm});
            skLineSegment(sketch, "E340", {"start": v(7.95, -61.3) * mm, "end": v(10.78, -61.2) * mm});
            skLineSegment(sketch, "E341", {"start": v(10.78, -61.2) * mm, "end": v(14.17, -59.32) * mm});
            skLineSegment(sketch, "E342", {"start": v(14.17, -59.32) * mm, "end": v(16.22, -56.86) * mm});
            skLineSegment(sketch, "E343", {"start": v(16.22, -56.86) * mm, "end": v(17.06, -52.66) * mm});
            skLineSegment(sketch, "E344", {"start": v(17.06, -52.66) * mm, "end": v(17.25, -49.33) * mm});
            skLineSegment(sketch, "E345", {"start": v(17.25, -49.33) * mm, "end": v(16.8, -44.46) * mm});
            skLineSegment(sketch, "E346", {"start": v(16.8, -44.46) * mm, "end": v(15.56, -38.79) * mm});
            skLineSegment(sketch, "E347", {"start": v(15.56, -38.79) * mm, "end": v(14.66, -33.6) * mm});
            skLineSegment(sketch, "E348", {"start": v(14.66, -33.6) * mm, "end": v(14.17, -29.64) * mm});
            skLineSegment(sketch, "E349", {"start": v(14.17, -29.64) * mm, "end": v(15.6, -23.03) * mm});
            skLineSegment(sketch, "E350", {"start": v(15.6, -23.03) * mm, "end": v(17.34, -19.4) * mm});
            skLineSegment(sketch, "E351", {"start": v(17.34, -19.4) * mm, "end": v(19.47, -15.5) * mm});
            skLineSegment(sketch, "E352", {"start": v(19.47, -15.5) * mm, "end": v(22.34, -11.74) * mm});
            skLineSegment(sketch, "E353", {"start": v(22.34, -11.74) * mm, "end": v(25.21, -8.8) * mm});
            skLineSegment(sketch, "E354", {"start": v(25.21, -8.8) * mm, "end": v(28.32, -5.7) * mm});
            skLineSegment(sketch, "E355", {"start": v(28.32, -5.7) * mm, "end": v(31.28, -3.08) * mm});
            skLineSegment(sketch, "E356", {"start": v(31.28, -3.08) * mm, "end": v(34.77, 0.16) * mm});
            skLineSegment(sketch, "E357", {"start": v(34.77, 0.16) * mm, "end": v(37.83, 2.93) * mm});
            skLineSegment(sketch, "E358", {"start": v(37.83, 2.93) * mm, "end": v(41.66, 6.39) * mm});
            skLineSegment(sketch, "E359", {"start": v(41.66, 6.39) * mm, "end": v(45.73, 10.65) * mm});
            skLineSegment(sketch, "E360", {"start": v(45.73, 10.65) * mm, "end": v(49.75, 14.74) * mm});
            skLineSegment(sketch, "E361", {"start": v(49.75, 14.74) * mm, "end": v(51.97, 17.54) * mm});
            skLineSegment(sketch, "E362", {"start": v(51.97, 17.54) * mm, "end": v(54.34, 20.28) * mm});
            skLineSegment(sketch, "E363", {"start": v(54.34, 20.28) * mm, "end": v(55.95, 23.37) * mm});
            skLineSegment(sketch, "E364", {"start": v(55.95, 23.37) * mm, "end": v(57.17, 26.64) * mm});
            skLineSegment(sketch, "E365", {"start": v(57.17, 26.64) * mm, "end": v(57.93, 30.53) * mm});
            skLineSegment(sketch, "E366", {"start": v(57.93, 30.53) * mm, "end": v(58.6, 34.47) * mm});
            skLineSegment(sketch, "E367", {"start": v(58.6, 34.47) * mm, "end": v(58.35, 38.41) * mm});
            skLineSegment(sketch, "E368", {"start": v(58.35, 38.41) * mm, "end": v(57.48, 42.52) * mm});
            skLineSegment(sketch, "E369", {"start": v(57.48, 42.52) * mm, "end": v(56.95, 46.2) * mm});
            skLineSegment(sketch, "E370", {"start": v(56.95, 46.2) * mm, "end": v(57.52, 51.64) * mm});
            skLineSegment(sketch, "E371", {"start": v(57.52, 51.64) * mm, "end": v(57.52, 55.75) * mm});
            skLineSegment(sketch, "E372", {"start": v(57.52, 55.75) * mm, "end": v(57.01, 58.96) * mm});
            skLineSegment(sketch, "E373", {"start": v(57.01, 58.96) * mm, "end": v(56.2, 60.2) * mm});
            skLineSegment(sketch, "E374", {"start": v(56.2, 60.2) * mm, "end": v(54.97, 60.21) * mm});
            skLineSegment(sketch, "E375", {"start": v(54.97, 60.21) * mm, "end": v(53.14, 58.84) * mm});
            skLineSegment(sketch, "E376", {"start": v(53.14, 58.84) * mm, "end": v(51.34, 55.82) * mm});
            skLineSegment(sketch, "E377", {"start": v(51.34, 55.82) * mm, "end": v(49.65, 50.93) * mm});
            skLineSegment(sketch, "E378", {"start": v(49.65, 50.93) * mm, "end": v(49.05, 46.09) * mm});
            skLineSegment(sketch, "E379", {"start": v(49.05, 46.09) * mm, "end": v(48.51, 40.92) * mm});
            skLineSegment(sketch, "E380", {"start": v(48.51, 40.92) * mm, "end": v(48.15, 36.52) * mm});
            skLineSegment(sketch, "E381", {"start": v(48.15, 36.52) * mm, "end": v(46.78, 32.07) * mm});
            skLineSegment(sketch, "E382", {"start": v(46.78, 32.07) * mm, "end": v(45.36, 29.66) * mm});
            skLineSegment(sketch, "E383", {"start": v(45.36, 29.66) * mm, "end": v(43.78, 27.18) * mm});
            skLineSegment(sketch, "E384", {"start": v(43.78, 27.18) * mm, "end": v(41.09, 25.4) * mm});
            skLineSegment(sketch, "E385", {"start": v(41.09, 25.4) * mm, "end": v(36.5, 23.38) * mm});
            skLineSegment(sketch, "E386", {"start": v(36.5, 23.38) * mm, "end": v(32.02, 22.34) * mm});
            skLineSegment(sketch, "E387", {"start": v(32.02, 22.34) * mm, "end": v(27.7, 21.49) * mm});
            skLineSegment(sketch, "E388", {"start": v(27.7, 21.49) * mm, "end": v(21.56, 20.8) * mm});
            skLineSegment(sketch, "E389", {"start": v(21.56, 20.8) * mm, "end": v(17.54, 21.02) * mm});
            skLineSegment(sketch, "E390", {"start": v(17.54, 21.02) * mm, "end": v(13.51, 21.73) * mm});
            skLineSegment(sketch, "E391", {"start": v(13.51, 21.73) * mm, "end": v(11.17, 21.73) * mm});
            skLineSegment(sketch, "E392", {"start": v(11.17, 21.73) * mm, "end": v(8.93, 20.63) * mm});
            skLineSegment(sketch, "E393", {"start": v(8.93, 20.63) * mm, "end": v(6.97, 18.07) * mm});
            skLineSegment(sketch, "E394", {"start": v(6.97, 18.07) * mm, "end": v(6.72, 13.34) * mm});
            skLineSegment(sketch, "E395", {"start": v(6.72, 13.34) * mm, "end": v(6.6, 11.08) * mm});
            skLineSegment(sketch, "E396", {"start": v(6.6, 11.08) * mm, "end": v(5.62, 5.07) * mm});
            skLineSegment(sketch, "E397", {"start": v(5.62, 5.07) * mm, "end": v(4.1, 0.44) * mm});
            skLineSegment(sketch, "E398", {"start": v(4.1, 0.44) * mm, "end": v(2.65, -2.5) * mm});
            skLineSegment(sketch, "E399", {"start": v(2.65, -2.5) * mm, "end": v(0.45, -5.14) * mm});
            skLineSegment(sketch, "E400", {"start": v(0.45, -5.14) * mm, "end": v(0.11, -5.42) * mm});
            skLineSegment(sketch, "E401.MirrorCS", {"start": v(-0.45, -5.14) * mm, "end": v(-0.11, -5.42) * mm});
            skLineSegment(sketch, "E402.MirrorCS", {"start": v(-2.65, -2.5) * mm, "end": v(-0.45, -5.14) * mm});
            skLineSegment(sketch, "E403.MirrorCS", {"start": v(-4.1, 0.44) * mm, "end": v(-2.65, -2.5) * mm});
            skLineSegment(sketch, "E404.MirrorCS", {"start": v(-5.62, 5.07) * mm, "end": v(-4.1, 0.44) * mm});
            skLineSegment(sketch, "E405.MirrorCS", {"start": v(-6.6, 11.08) * mm, "end": v(-5.62, 5.07) * mm});
            skLineSegment(sketch, "E406.MirrorCS", {"start": v(-6.72, 13.34) * mm, "end": v(-6.6, 11.08) * mm});
            skLineSegment(sketch, "E407.MirrorCS", {"start": v(-6.97, 18.07) * mm, "end": v(-6.72, 13.34) * mm});
            skLineSegment(sketch, "E408.MirrorCS", {"start": v(-8.93, 20.63) * mm, "end": v(-6.97, 18.07) * mm});
            skLineSegment(sketch, "E409.MirrorCS", {"start": v(-11.17, 21.73) * mm, "end": v(-8.93, 20.63) * mm});
            skLineSegment(sketch, "E410.MirrorCS", {"start": v(-13.51, 21.73) * mm, "end": v(-11.17, 21.73) * mm});
            skLineSegment(sketch, "E411.MirrorCS", {"start": v(-17.54, 21.02) * mm, "end": v(-13.51, 21.73) * mm});
            skLineSegment(sketch, "E412.MirrorCS", {"start": v(-21.56, 20.8) * mm, "end": v(-17.54, 21.02) * mm});
            skLineSegment(sketch, "E413.MirrorCS", {"start": v(-27.7, 21.49) * mm, "end": v(-21.56, 20.8) * mm});
            skLineSegment(sketch, "E414.MirrorCS", {"start": v(-32.02, 22.34) * mm, "end": v(-27.7, 21.49) * mm});
            skLineSegment(sketch, "E415.MirrorCS", {"start": v(-36.5, 23.38) * mm, "end": v(-32.02, 22.34) * mm});
            skLineSegment(sketch, "E416.MirrorCS", {"start": v(-41.09, 25.4) * mm, "end": v(-36.5, 23.38) * mm});
            skLineSegment(sketch, "E417.MirrorCS", {"start": v(-43.78, 27.18) * mm, "end": v(-41.09, 25.4) * mm});
            skLineSegment(sketch, "E418.MirrorCS", {"start": v(-46.78, 32.07) * mm, "end": v(-45.36, 29.66) * mm});
            skLineSegment(sketch, "E419.MirrorCS", {"start": v(-48.15, 36.52) * mm, "end": v(-46.78, 32.07) * mm});
            skLineSegment(sketch, "E420.MirrorCS", {"start": v(-48.51, 40.92) * mm, "end": v(-48.15, 36.52) * mm});
            skLineSegment(sketch, "E421.MirrorCS", {"start": v(-49.05, 46.09) * mm, "end": v(-48.51, 40.92) * mm});
            skLineSegment(sketch, "E422.MirrorCS", {"start": v(-49.65, 50.93) * mm, "end": v(-49.05, 46.09) * mm});
            skLineSegment(sketch, "E423.MirrorCS", {"start": v(-51.34, 55.82) * mm, "end": v(-49.65, 50.93) * mm});
            skLineSegment(sketch, "E424.MirrorCS", {"start": v(-53.14, 58.84) * mm, "end": v(-51.34, 55.82) * mm});
            skLineSegment(sketch, "E425.MirrorCS", {"start": v(-54.97, 60.21) * mm, "end": v(-53.14, 58.84) * mm});
            skLineSegment(sketch, "E426.MirrorCS", {"start": v(-56.2, 60.2) * mm, "end": v(-54.97, 60.21) * mm});
            skLineSegment(sketch, "E427.MirrorCS", {"start": v(-57.01, 58.96) * mm, "end": v(-56.2, 60.2) * mm});
            skLineSegment(sketch, "E428.MirrorCS", {"start": v(-57.52, 55.75) * mm, "end": v(-57.01, 58.96) * mm});
            skLineSegment(sketch, "E429.MirrorCS", {"start": v(-57.52, 51.64) * mm, "end": v(-57.52, 55.75) * mm});
            skLineSegment(sketch, "E430.MirrorCS", {"start": v(-56.95, 46.2) * mm, "end": v(-57.52, 51.64) * mm});
            skLineSegment(sketch, "E431.MirrorCS", {"start": v(-57.48, 42.52) * mm, "end": v(-56.95, 46.2) * mm});
            skLineSegment(sketch, "E432.MirrorCS", {"start": v(-58.35, 38.41) * mm, "end": v(-57.48, 42.52) * mm});
            skLineSegment(sketch, "E433.MirrorCS", {"start": v(-58.6, 34.47) * mm, "end": v(-58.35, 38.41) * mm});
            skLineSegment(sketch, "E434.MirrorCS", {"start": v(-57.93, 30.53) * mm, "end": v(-58.6, 34.47) * mm});
            skLineSegment(sketch, "E435.MirrorCS", {"start": v(-57.17, 26.64) * mm, "end": v(-57.93, 30.53) * mm});
            skLineSegment(sketch, "E436.MirrorCS", {"start": v(-55.95, 23.37) * mm, "end": v(-57.17, 26.64) * mm});
            skLineSegment(sketch, "E437.MirrorCS", {"start": v(-54.34, 20.28) * mm, "end": v(-55.95, 23.37) * mm});
            skLineSegment(sketch, "E438.MirrorCS", {"start": v(-51.97, 17.54) * mm, "end": v(-54.34, 20.28) * mm});
            skLineSegment(sketch, "E439.MirrorCS", {"start": v(-49.75, 14.74) * mm, "end": v(-51.97, 17.54) * mm});
            skLineSegment(sketch, "E440.MirrorCS", {"start": v(-45.73, 10.65) * mm, "end": v(-49.75, 14.74) * mm});
            skLineSegment(sketch, "E441.MirrorCS", {"start": v(-41.66, 6.39) * mm, "end": v(-45.73, 10.65) * mm});
            skLineSegment(sketch, "E442.MirrorCS", {"start": v(-34.77, 0.16) * mm, "end": v(-37.83, 2.93) * mm});
            skLineSegment(sketch, "E443.MirrorCS", {"start": v(-31.28, -3.08) * mm, "end": v(-34.77, 0.16) * mm});
            skLineSegment(sketch, "E444.MirrorCS", {"start": v(-28.32, -5.7) * mm, "end": v(-31.28, -3.08) * mm});
            skLineSegment(sketch, "E445.MirrorCS", {"start": v(-25.21, -8.8) * mm, "end": v(-28.32, -5.7) * mm});
            skLineSegment(sketch, "E446.MirrorCS", {"start": v(-22.34, -11.74) * mm, "end": v(-25.21, -8.8) * mm});
            skLineSegment(sketch, "E447.MirrorCS", {"start": v(-19.47, -15.5) * mm, "end": v(-22.34, -11.74) * mm});
            skLineSegment(sketch, "E448.MirrorCS", {"start": v(-17.34, -19.4) * mm, "end": v(-19.47, -15.5) * mm});
            skLineSegment(sketch, "E449.MirrorCS", {"start": v(-15.6, -23.03) * mm, "end": v(-17.34, -19.4) * mm});
            skLineSegment(sketch, "E450.MirrorCS", {"start": v(-14.17, -29.64) * mm, "end": v(-15.6, -23.03) * mm});
            skLineSegment(sketch, "E451.MirrorCS", {"start": v(-14.66, -33.6) * mm, "end": v(-14.17, -29.64) * mm});
            skLineSegment(sketch, "E452.MirrorCS", {"start": v(-15.56, -38.79) * mm, "end": v(-14.66, -33.6) * mm});
            skLineSegment(sketch, "E453.MirrorCS", {"start": v(-16.8, -44.46) * mm, "end": v(-15.56, -38.79) * mm});
            skLineSegment(sketch, "E454.MirrorCS", {"start": v(-17.25, -49.33) * mm, "end": v(-16.8, -44.46) * mm});
            skLineSegment(sketch, "E455.MirrorCS", {"start": v(-17.06, -52.66) * mm, "end": v(-17.25, -49.33) * mm});
            skLineSegment(sketch, "E456.MirrorCS", {"start": v(-16.22, -56.86) * mm, "end": v(-17.06, -52.66) * mm});
            skLineSegment(sketch, "E457.MirrorCS", {"start": v(-14.17, -59.32) * mm, "end": v(-16.22, -56.86) * mm});
            skLineSegment(sketch, "E458.MirrorCS", {"start": v(-10.78, -61.2) * mm, "end": v(-14.17, -59.32) * mm});
            skLineSegment(sketch, "E459.MirrorCS", {"start": v(-7.95, -61.3) * mm, "end": v(-10.78, -61.2) * mm});
            skLineSegment(sketch, "E460.MirrorCS", {"start": v(-5.28, -60.82) * mm, "end": v(-7.95, -61.3) * mm});
            skLineSegment(sketch, "E461.MirrorCS", {"start": v(-2.56, -60.82) * mm, "end": v(-5.28, -60.82) * mm});
            skLineSegment(sketch, "E462.MirrorCS", {"start": v(0, -60.82) * mm, "end": v(-2.56, -60.82) * mm});
            skLineSegment(sketch, "E463.MirrorCS", {"start": v(-45.36, 29.66) * mm, "end": v(-43.78, 27.18) * mm});
            skLineSegment(sketch, "E464", {"start": v(-41.66, 6.39) * mm, "end": v(-37.83, 2.93) * mm});
            skLineSegment(sketch, "E465", {"start": v(0.11, -5.42) * mm, "end": v(-0.11, -5.42) * mm});
            skSolve(sketch);
        }
        {
            var Q0;
            Q0=makeQuery(id+"F0.imprint","IMPRINT",FACE,{"disambiguationData":[TD([[makeQuery(id+"F0.imprint","IMPRINT",EDGE,{"derivedFrom":sQuery(id+"F0.wireOp",EDGE,"E76")}),-1.0]])]});
            extrude(context, id + "F1", {"entities" : qUnion([Q0]), "depth" : 25.4 * mm, "offsetDistance" : 25.4 * mm});
        }
        {
            var Q0;
            Q0=makeQuery(id+"F0.imprint","IMPRINT",FACE,{"disambiguationData":[TD([[makeQuery(id+"F0.imprint","IMPRINT",EDGE,{"derivedFrom":sQuery(id+"F0.wireOp",EDGE,"E102")}),-1.0]])]});
            var Q1;
            Q1=makeQuery(id+"F0.imprint","IMPRINT",FACE,{"disambiguationData":[TD([[makeQuery(id+"F0.imprint","IMPRINT",EDGE,{"derivedFrom":sQuery(id+"F0.wireOp",EDGE,"E227.MirrorCS")}),-1.0]])]});
            var Q2;
            Q2=makeQuery(id+"F0.imprint","IMPRINT",FACE,{"disambiguationData":[TD([[makeQuery(id+"F0.imprint","IMPRINT",EDGE,{"derivedFrom":sQuery(id+"F0.wireOp",EDGE,"E76")}),1.0]])]});
            var Q3;
            Q3=makeQuery(id+"F0.imprint","IMPRINT",FACE,{"disambiguationData":[TD([[makeQuery(id+"F0.imprint","IMPRINT",EDGE,{"derivedFrom":sQuery(id+"F0.wireOp",EDGE,"E90")}),-1.0]])]});
            var Q4;
            Q4=makeQuery(id+"F0.imprint","IMPRINT",FACE,{"disambiguationData":[TD([[makeQuery(id+"F0.imprint","IMPRINT",EDGE,{"derivedFrom":sQuery(id+"F0.wireOp",EDGE,"E180.MirrorCS")}),1.0]])]});
            extrude(context, id + "F2", {"entities" : qUnion([Q0, Q1, Q2, Q3, Q4]), "operationType" : NewBodyOperationType.ADD, "depth" : 6.35 * mm, "offsetDistance" : 25.4 * mm});
        }
        {
            var Q0;
            Q0=makeQuery(id+"F0.imprint","IMPRINT",FACE,{"disambiguationData":[TD([[makeQuery(id+"F0.imprint","IMPRINT",EDGE,{"derivedFrom":sQuery(id+"F0.wireOp",EDGE,"E0")}),1.0]])]});
            extrude(context, id + "F3", {"entities" : qUnion([Q0]), "operationType" : NewBodyOperationType.ADD, "depth" : 25.4 * mm, "offsetDistance" : 25.4 * mm});
        }
    });
